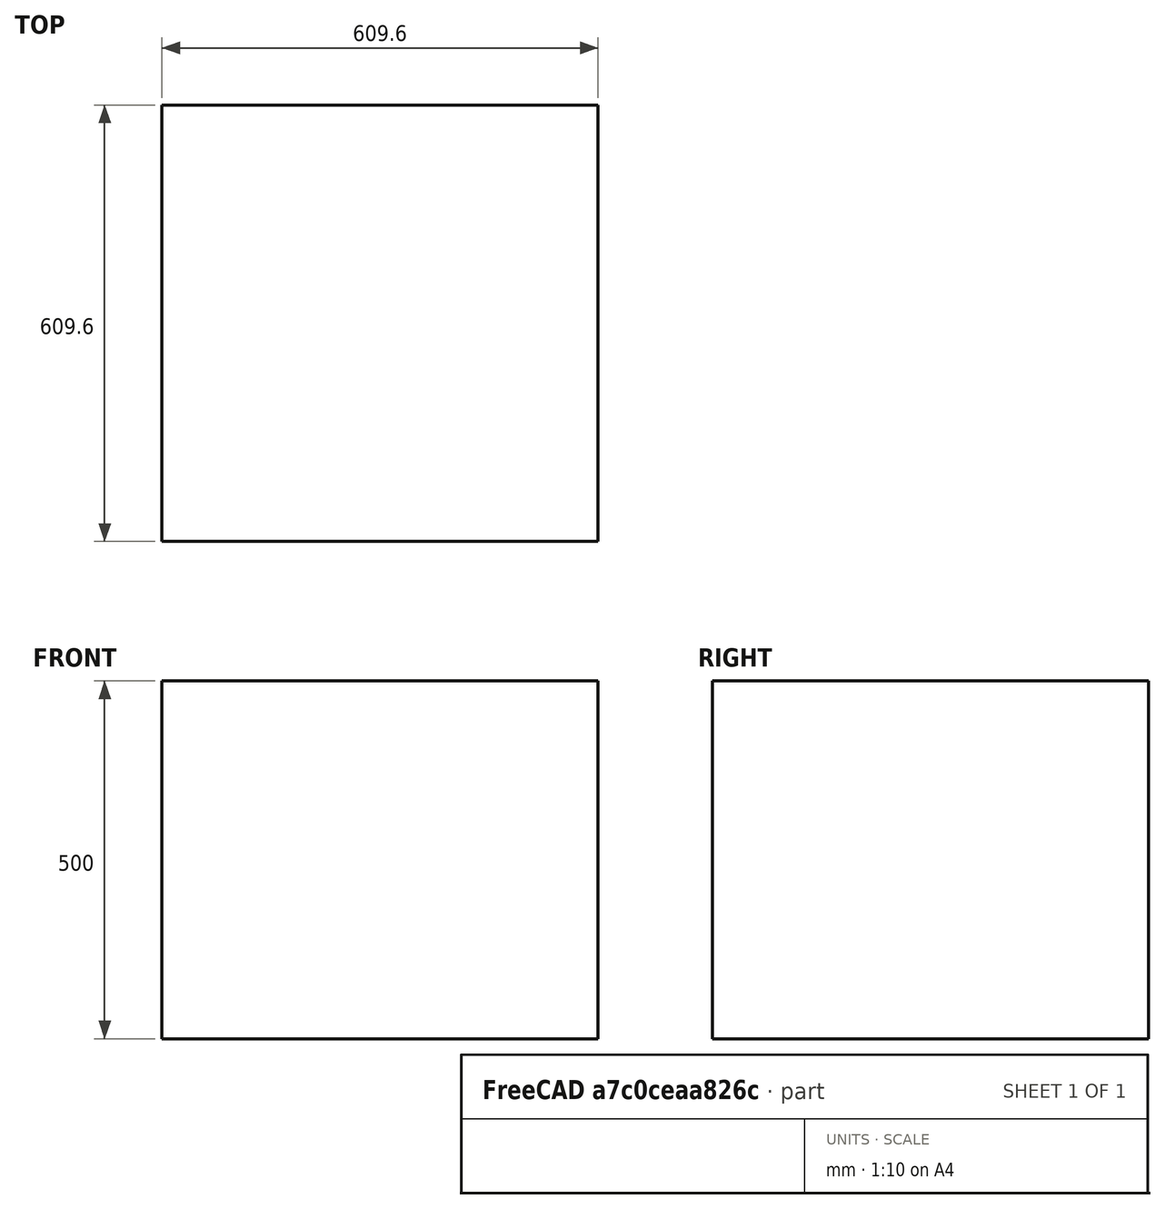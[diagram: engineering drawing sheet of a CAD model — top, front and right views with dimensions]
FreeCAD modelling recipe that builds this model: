
FCSTD DOCUMENT  (FreeCAD 1.0R39319 (Git))
Label: Box-VarSet-Example
License: All rights reserved
LicenseURL: https://en.wikipedia.org/wiki/All_rights_reserved
objects: Part::Box×1, App::VarSet×1
note: 1 computed .brp shape members not serialized (recipe doc carries the construction recipe); baked Part::Feature solids carry a one-line shape summary decoded from their .brp

FEATURE [Part::Box] Box  label="Cube"
  AttacherType = Attacher::AttachEngine3D
  Height = 500
  Length = 609.6
  Width = 609.6
  expr: Height = <<PQs>>.Base_H
  expr: Length = <<PQs>>.Base_L
  expr: Width = <<PQs>>.Base_W
FEATURE [App::VarSet] VarSet  label="PQs"
  ArticleID = 3MAV4GNFQ-3FU
  ArticleTitle = calc for freecad demo 1: (LxWxH, rho) => (V, m)
  Base_H = 500
  Base_L = 609.6
  Base_Q = 0
  Base_Rho = 0
  Base_V = 0
  Base_W = 609.6
  Base_m = 362.874
  CalcsLiveMappings = {\n  "docVersion": "0.2",\n  "unitsSchema": "UserPreferred",\n  "params": [],\n  "articles": [\n    {\n      "articleId": "3MAV4GNFQ-3FU",\n      "articleTitle": "calc for freecad demo 1: (LxWxH, rho) => (V, m)",\n      "lastUpdated": "2025-10-31T20:59:52.790Z",\n      "paramMappings": {\n        "Base_L": {\n          "pqSymbol": "L",\n          "pqExpression": null,\n          "pqFaceValue": 0.6095999999999999,\n          "pqFaceUnit": "m",\n          "pqBaseUnit": "m"\n        },\n        "Base_W": {\n          "pqSymbol": "W",\n          "pqExpression": null,\n          "pqFaceValue": 0.6095999999999999,\n          "pqFaceUnit": "m",\n          "pqBaseUnit": "m"\n        },\n        "Base_m": {\n          "pqSymbol": "m",\n          "pqExpression": "rho * V",\n          "pqFaceValue": 362.873896,\n          "pqFaceUnit": "kg",\n          "pqBaseUnit": "kg"\n        }\n      }\n    }\n  ]\n}
